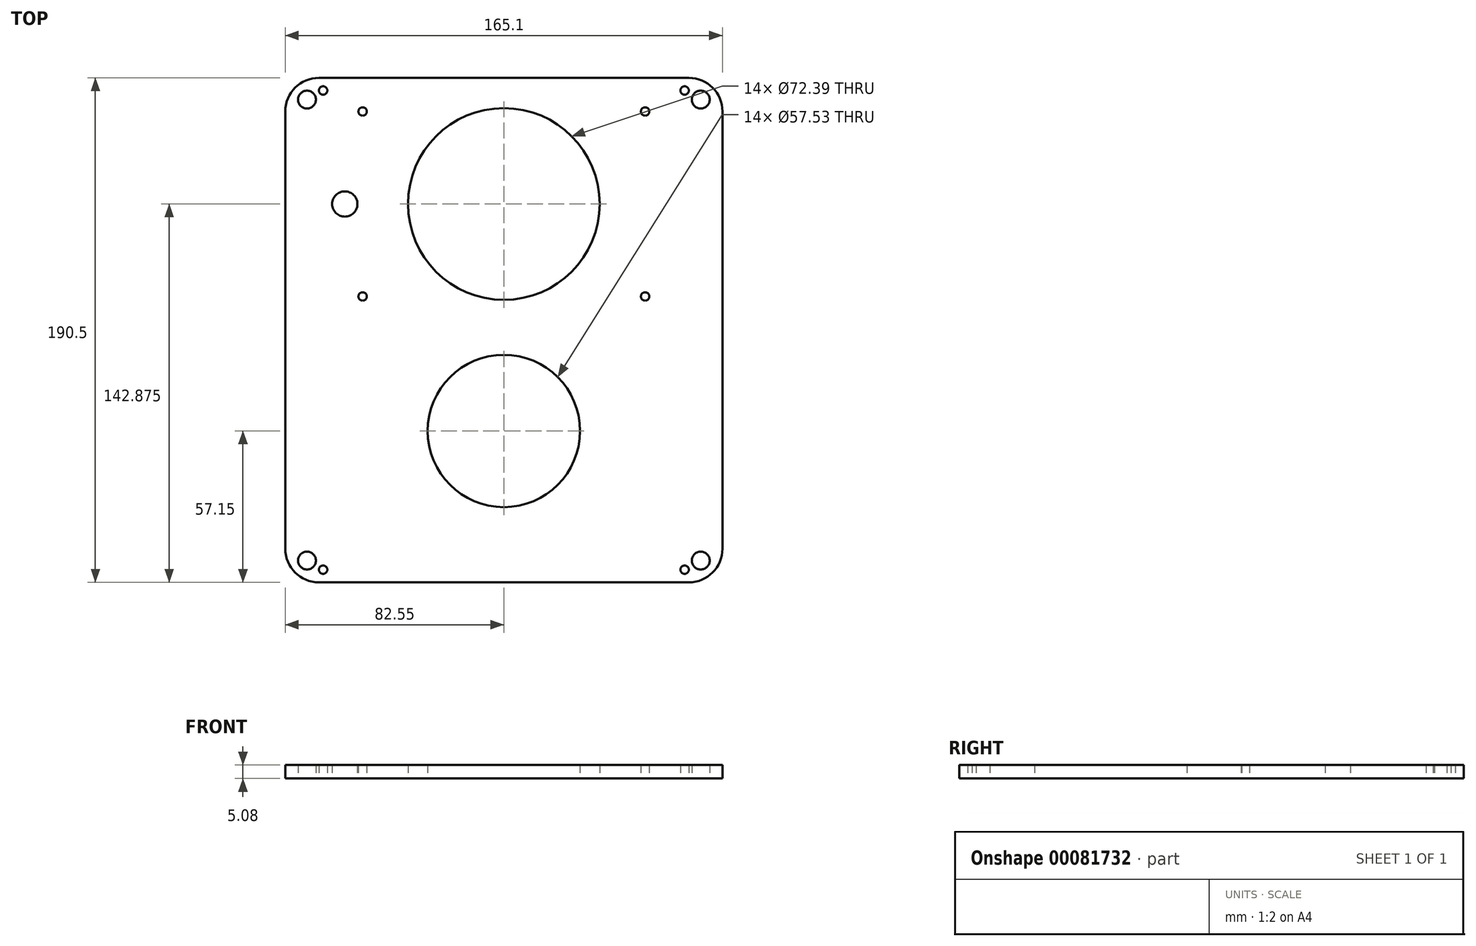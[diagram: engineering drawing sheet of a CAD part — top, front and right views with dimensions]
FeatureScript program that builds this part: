
annotation { "Feature Type Name" : "Feature", "Feature Type Description" : "" }
export const myFeature = defineFeature(function(context is Context, id is Id, definition is map)
    precondition{}
    {
        {
            var Q0;
            Q0=qCreatedBy(makeId("Top.planeOp"),FACE);
            var sketch = newSketch(context, id + "F0", { "sketchPlane" : qUnion([Q0])});
            skLineSegment(sketch, "E0.bottom", {"start": v(12.7, 0) * mm, "end": v(152.4, 0) * mm});
            skLineSegment(sketch, "E0.top", {"start": v(12.7, -190.5) * mm, "end": v(152.4, -190.5) * mm});
            skLineSegment(sketch, "E0.left", {"start": v(0, -12.7) * mm, "end": v(0, -177.8) * mm});
            skLineSegment(sketch, "E0.right", {"start": v(165.1, -12.7) * mm, "end": v(165.1, -177.8) * mm});
            skCircle(sketch, "E1", {"center": v(82.55, -47.63) * mm, "radius": 36.2 * mm});
            skCircle(sketch, "E2", {"center": v(82.55, -133.35) * mm, "radius": 28.77 * mm});
            skPoint(sketch, "E3.visualSharp", {"position": v(0, 0) * mm});
            skArc(sketch, "E3.filletArc", {"start": v(12.7, 0) * mm, "mid": v(3.72, -3.72) * mm, "end": v(0, -12.7) * mm});
            skPoint(sketch, "E4.visualSharp", {"position": v(165.1, 0) * mm});
            skArc(sketch, "E4.filletArc", {"start": v(165.1, -12.7) * mm, "mid": v(161.38, -3.72) * mm, "end": v(152.4, 0) * mm});
            skPoint(sketch, "E5.visualSharp", {"position": v(165.1, -190.5) * mm});
            skArc(sketch, "E5.filletArc", {"start": v(152.4, -190.5) * mm, "mid": v(161.38, -186.78) * mm, "end": v(165.1, -177.8) * mm});
            skPoint(sketch, "E6.visualSharp", {"position": v(0, -190.5) * mm});
            skArc(sketch, "E6.filletArc", {"start": v(0, -177.8) * mm, "mid": v(3.72, -186.78) * mm, "end": v(12.7, -190.5) * mm});
            skLineSegment(sketch, "E7.bottom", {"start": v(31.75, 0) * mm, "end": v(133.35, 0) * mm, "construction": true});
            skLineSegment(sketch, "E7.top", {"start": v(31.75, -95.25) * mm, "end": v(133.35, -95.25) * mm, "construction": true});
            skLineSegment(sketch, "E7.left", {"start": v(31.75, 0) * mm, "end": v(31.75, -95.25) * mm, "construction": true});
            skLineSegment(sketch, "E7.right", {"start": v(133.35, 0) * mm, "end": v(133.35, -95.25) * mm, "construction": true});
            skSolve(sketch);
        }
        {
            var Q0;
            Q0 = qSketchRegion(id + "F0", true);
            extrude(context, id + "F1", {"entities" : qUnion([Q0]), "depth" : 5.08 * mm});
        }
        {
            var Q0;
            Q0=makeQuery(id+"F1.opExtrude","CAP_FACE",FACE,{"disambiguationData":[OSD([sQuery(id+"F0.wireOp",EDGE,"E0.bottom"),sQuery(id+"F0.wireOp",EDGE,"E0.top"),sQuery(id+"F0.wireOp",EDGE,"E0.left"),sQuery(id+"F0.wireOp",EDGE,"E0.right"),sQuery(id+"F0.wireOp",EDGE,"E1"),sQuery(id+"F0.wireOp",EDGE,"E2"),sQuery(id+"F0.wireOp",EDGE,"tNX6zDZ8-l4rx-qWVM-tXeO-O2qndWeJSTiN"),sQuery(id+"F0.wireOp",EDGE,"E3.filletArc"),sQuery(id+"F0.wireOp",EDGE,"E4.filletArc"),sQuery(id+"F0.wireOp",EDGE,"E5.filletArc"),sQuery(id+"F0.wireOp",EDGE,"E6.filletArc")])],"isStart":false});
            var sketch = newSketch(context, id + "F2", { "sketchPlane" : qUnion([Q0])});
            skLineSegment(sketch, "E8", {"start": v(0, 0) * mm, "end": v(35.65, -35.65) * mm, "construction": true});
            skLineSegment(sketch, "E9", {"start": v(0, 0) * mm, "end": v(0, -45.25) * mm, "construction": true});
            skLineSegment(sketch, "E10", {"start": v(165.1, -136.66) * mm, "end": v(165.1, -190.5) * mm, "construction": true});
            skLineSegment(sketch, "E11", {"start": v(165.1, -190.5) * mm, "end": v(130.86, -156.26) * mm, "construction": true});
            skLineSegment(sketch, "E12", {"start": v(0, -130.44) * mm, "end": v(0, -190.5) * mm, "construction": true});
            skLineSegment(sketch, "E13", {"start": v(0, -190.5) * mm, "end": v(31.66, -158.84) * mm, "construction": true});
            skLineSegment(sketch, "E14", {"start": v(165.1, -38.7) * mm, "end": v(165.1, 0) * mm, "construction": true});
            skLineSegment(sketch, "E15", {"start": v(165.1, 0) * mm, "end": v(130.8, -34.3) * mm, "construction": true});
            skPoint(sketch, "E16", {"position": v(156.9, -8.2) * mm});
            skPoint(sketch, "E17", {"position": v(8.2, -182.3) * mm});
            skPoint(sketch, "E18", {"position": v(156.9, -182.3) * mm});
            skPoint(sketch, "E19", {"position": v(8.2, -8.2) * mm});
            skSolve(sketch);
        }
        {
            var Q0;
            Q0=sQuery(id+"F2.wireOp",VERTEX,"E19");
            var Q1;
            Q1=sQuery(id+"F2.wireOp",VERTEX,"E16");
            var Q2;
            Q2=sQuery(id+"F2.wireOp",VERTEX,"E18");
            var Q3;
            Q3=sQuery(id+"F2.wireOp",VERTEX,"E17");
            var Q4;
            Q4=makeQuery(id+"F1.opExtrude","SWEPT_BODY",BODY,{"disambiguationData":[OSD([sQuery(id+"F0.wireOp",EDGE,"E0.bottom"),sQuery(id+"F0.wireOp",EDGE,"E0.top"),sQuery(id+"F0.wireOp",EDGE,"E0.left"),sQuery(id+"F0.wireOp",EDGE,"E0.right"),sQuery(id+"F0.wireOp",EDGE,"E1"),sQuery(id+"F0.wireOp",EDGE,"E2"),sQuery(id+"F0.wireOp",EDGE,"tNX6zDZ8-l4rx-qWVM-tXeO-O2qndWeJSTiN"),sQuery(id+"F0.wireOp",EDGE,"E3.filletArc"),sQuery(id+"F0.wireOp",EDGE,"E4.filletArc"),sQuery(id+"F0.wireOp",EDGE,"E5.filletArc"),sQuery(id+"F0.wireOp",EDGE,"E6.filletArc")])]});
            hole(context, id + "F3", {"style" : HoleStyle.SIMPLE, "endStyle" : HoleEndStyle.THROUGH, "standardTappedOrClearance" : lookupTablePath({ "standard" : "ANSI", "fit" : "Normal (ASME)", "size" : "1/4", "type" : "Clearance" }), "standardBlindInLast" : lookupTablePath({ "fit" : "Free", "standard" : "ANSI", "size" : "1/4", "type" : "Clearance" }), "holeDiameter" : 6.76 * mm, "locations" : qUnion([Q0, Q1, Q2, Q3]), "scope" : qUnion([Q4]), "isTappedThrough" : true, "startStyle" : HoleStartStyle.PART});
        }
        {
            var Q0;
            Q0=makeQuery(id+"F1.opExtrude","CAP_FACE",FACE,{"disambiguationData":[OSD([sQuery(id+"F0.wireOp",EDGE,"E0.bottom"),sQuery(id+"F0.wireOp",EDGE,"E0.top"),sQuery(id+"F0.wireOp",EDGE,"E0.left"),sQuery(id+"F0.wireOp",EDGE,"E0.right"),sQuery(id+"F0.wireOp",EDGE,"E1"),sQuery(id+"F0.wireOp",EDGE,"E2"),sQuery(id+"F0.wireOp",EDGE,"tNX6zDZ8-l4rx-qWVM-tXeO-O2qndWeJSTiN"),sQuery(id+"F0.wireOp",EDGE,"E3.filletArc"),sQuery(id+"F0.wireOp",EDGE,"E4.filletArc"),sQuery(id+"F0.wireOp",EDGE,"E5.filletArc"),sQuery(id+"F0.wireOp",EDGE,"E6.filletArc")])],"isStart":false});
            var sketch = newSketch(context, id + "F4", { "sketchPlane" : qUnion([Q0])});
            skPoint(sketch, "E20", {"position": v(14.29, -185.72) * mm});
            skPoint(sketch, "E21", {"position": v(150.81, -185.72) * mm});
            skPoint(sketch, "E22", {"position": v(150.81, -4.78) * mm});
            skPoint(sketch, "E23", {"position": v(14.29, -4.78) * mm});
            skSolve(sketch);
        }
        {
            var Q0;
            Q0=sQuery(id+"F4.wireOp",VERTEX,"E20");
            var Q1;
            Q1=sQuery(id+"F4.wireOp",VERTEX,"E21");
            var Q2;
            Q2=sQuery(id+"F4.wireOp",VERTEX,"E22");
            var Q3;
            Q3=sQuery(id+"F4.wireOp",VERTEX,"E23");
            var Q4;
            Q4=makeQuery(id+"F1.opExtrude","SWEPT_BODY",BODY,{"disambiguationData":[OSD([sQuery(id+"F0.wireOp",EDGE,"E0.bottom"),sQuery(id+"F0.wireOp",EDGE,"E0.top"),sQuery(id+"F0.wireOp",EDGE,"E0.left"),sQuery(id+"F0.wireOp",EDGE,"E0.right"),sQuery(id+"F0.wireOp",EDGE,"E1"),sQuery(id+"F0.wireOp",EDGE,"E2"),sQuery(id+"F0.wireOp",EDGE,"tNX6zDZ8-l4rx-qWVM-tXeO-O2qndWeJSTiN"),sQuery(id+"F0.wireOp",EDGE,"E3.filletArc"),sQuery(id+"F0.wireOp",EDGE,"E4.filletArc"),sQuery(id+"F0.wireOp",EDGE,"E5.filletArc"),sQuery(id+"F0.wireOp",EDGE,"E6.filletArc")])]});
            hole(context, id + "F5", {"style" : HoleStyle.SIMPLE, "endStyle" : HoleEndStyle.THROUGH, "holeDiameter" : 3.17 * mm, "locations" : qUnion([Q0, Q1, Q2, Q3]), "scope" : qUnion([Q4]), "isTappedThrough" : true, "startStyle" : HoleStartStyle.PART});
        }
        {
            var Q0;
            Q0=makeQuery(id+"F1.opExtrude","CAP_FACE",FACE,{"disambiguationData":[OSD([sQuery(id+"F0.wireOp",EDGE,"E0.bottom"),sQuery(id+"F0.wireOp",EDGE,"E0.top"),sQuery(id+"F0.wireOp",EDGE,"E0.left"),sQuery(id+"F0.wireOp",EDGE,"E0.right"),sQuery(id+"F0.wireOp",EDGE,"E1"),sQuery(id+"F0.wireOp",EDGE,"E2"),sQuery(id+"F0.wireOp",EDGE,"E3.filletArc"),sQuery(id+"F0.wireOp",EDGE,"E4.filletArc"),sQuery(id+"F0.wireOp",EDGE,"E5.filletArc"),sQuery(id+"F0.wireOp",EDGE,"E6.filletArc")])],"isStart":false});
            var sketch = newSketch(context, id + "F6", { "sketchPlane" : qUnion([Q0])});
            skLineSegment(sketch, "E24.bottom", {"start": v(31.75, 0) * mm, "end": v(133.35, 0) * mm, "construction": true});
            skLineSegment(sketch, "E24.top", {"start": v(31.75, -95.25) * mm, "end": v(133.35, -95.25) * mm, "construction": true});
            skLineSegment(sketch, "E24.left", {"start": v(31.75, 0) * mm, "end": v(31.75, -95.25) * mm, "construction": true});
            skLineSegment(sketch, "E24.right", {"start": v(133.35, 0) * mm, "end": v(133.35, -95.25) * mm, "construction": true});
            skPoint(sketch, "E25", {"position": v(29.21, -82.55) * mm});
            skPoint(sketch, "E26", {"position": v(29.21, -12.7) * mm});
            skPoint(sketch, "E27", {"position": v(135.9, -12.7) * mm});
            skPoint(sketch, "E28", {"position": v(135.9, -82.55) * mm});
            skSolve(sketch);
        }
        {
            var Q0;
            Q0=sQuery(id+"F6.wireOp",VERTEX,"E25");
            var Q1;
            Q1=sQuery(id+"F6.wireOp",VERTEX,"E26");
            var Q2;
            Q2=sQuery(id+"F6.wireOp",VERTEX,"E27");
            var Q3;
            Q3=sQuery(id+"F6.wireOp",VERTEX,"E28");
            var Q4;
            Q4=makeQuery(id+"F1.opExtrude","SWEPT_BODY",BODY,{"disambiguationData":[OSD([sQuery(id+"F0.wireOp",EDGE,"E0.bottom"),sQuery(id+"F0.wireOp",EDGE,"E0.top"),sQuery(id+"F0.wireOp",EDGE,"E0.left"),sQuery(id+"F0.wireOp",EDGE,"E0.right"),sQuery(id+"F0.wireOp",EDGE,"E1"),sQuery(id+"F0.wireOp",EDGE,"E2"),sQuery(id+"F0.wireOp",EDGE,"E3.filletArc"),sQuery(id+"F0.wireOp",EDGE,"E4.filletArc"),sQuery(id+"F0.wireOp",EDGE,"E5.filletArc"),sQuery(id+"F0.wireOp",EDGE,"E6.filletArc")])]});
            hole(context, id + "F7", {"style" : HoleStyle.SIMPLE, "endStyle" : HoleEndStyle.THROUGH, "holeDiameter" : 3.17 * mm, "locations" : qUnion([Q0, Q1, Q2, Q3]), "scope" : qUnion([Q4]), "isTappedThrough" : true, "startStyle" : HoleStartStyle.PART});
        }
        {
            var Q0;
            Q0=makeQuery(id+"F1.opExtrude","CAP_FACE",FACE,{"disambiguationData":[OSD([sQuery(id+"F0.wireOp",EDGE,"E0.bottom"),sQuery(id+"F0.wireOp",EDGE,"E0.top"),sQuery(id+"F0.wireOp",EDGE,"E0.left"),sQuery(id+"F0.wireOp",EDGE,"E0.right"),sQuery(id+"F0.wireOp",EDGE,"E1"),sQuery(id+"F0.wireOp",EDGE,"E2"),sQuery(id+"F0.wireOp",EDGE,"E3.filletArc"),sQuery(id+"F0.wireOp",EDGE,"E4.filletArc"),sQuery(id+"F0.wireOp",EDGE,"E5.filletArc"),sQuery(id+"F0.wireOp",EDGE,"E6.filletArc")])],"isStart":false});
            var sketch = newSketch(context, id + "F8", { "sketchPlane" : qUnion([Q0])});
            skPoint(sketch, "E29", {"position": v(22.48, -47.63) * mm});
            skSolve(sketch);
        }
        {
            var Q0;
            Q0=sQuery(id+"F8.wireOp",VERTEX,"E29");
            var Q1;
            Q1=makeQuery(id+"F1.opExtrude","SWEPT_BODY",BODY,{"disambiguationData":[OSD([sQuery(id+"F0.wireOp",EDGE,"E0.bottom"),sQuery(id+"F0.wireOp",EDGE,"E0.top"),sQuery(id+"F0.wireOp",EDGE,"E0.left"),sQuery(id+"F0.wireOp",EDGE,"E0.right"),sQuery(id+"F0.wireOp",EDGE,"E1"),sQuery(id+"F0.wireOp",EDGE,"E2"),sQuery(id+"F0.wireOp",EDGE,"E3.filletArc"),sQuery(id+"F0.wireOp",EDGE,"E4.filletArc"),sQuery(id+"F0.wireOp",EDGE,"E5.filletArc"),sQuery(id+"F0.wireOp",EDGE,"E6.filletArc")])]});
            hole(context, id + "F9", {"style" : HoleStyle.SIMPLE, "endStyle" : HoleEndStyle.THROUGH, "holeDiameter" : 9.52 * mm, "locations" : qUnion([Q0]), "scope" : qUnion([Q1]), "isTappedThrough" : true, "startStyle" : HoleStartStyle.PART});
        }
    });
